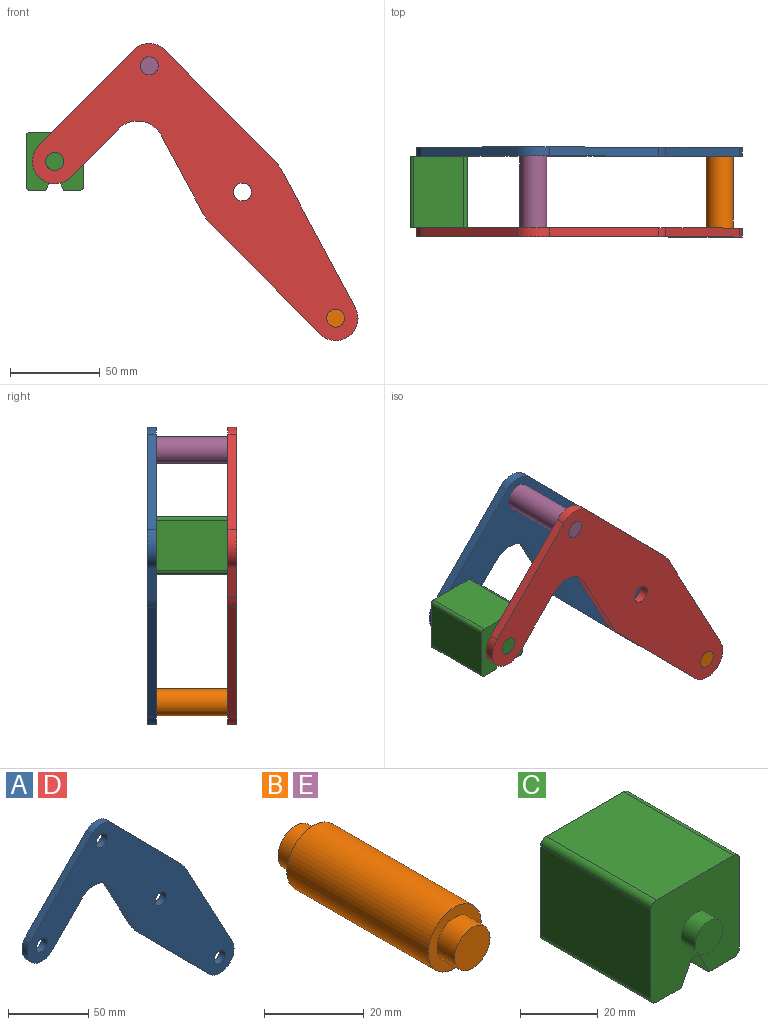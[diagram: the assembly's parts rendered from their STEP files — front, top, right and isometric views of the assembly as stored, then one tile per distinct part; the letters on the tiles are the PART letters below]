
ASSEMBLY  parts=5 mates=3
PART A: 18 faces, bbox 181.7x5x165.8 mm
  f0: plane 43.49x23.35mm, normal (-0.88,0,-0.47), area 246.8mm2, adj f1,f14,f16,f17
  f1: cylinder r=25mm len=5.75mm, axis (0,1,0), area 35.8mm2, adj f0,f2,f16,f17
  f2: plane 61.6x60.87mm, normal (-0.71,0,-0.7), area 433mm2, adj f1,f3,f16,f17
  f3: cylinder r=12.5mm len=21.39mm, axis (0,1,0), area 178.4mm2, adj f2,f4,f16,f17
  f4: plane 76.3x40.96mm, normal (0.88,0,0.47), area 433mm2, adj f3,f5,f16,f17
  f5: cylinder r=25mm len=5.75mm, axis (0,1,0), area 35.8mm2, adj f4,f6,f16,f17
  f6: plane 61.6x60.87mm, normal (0.71,0,0.7), area 433mm2, adj f5,f7,f16,f17
  f7: cylinder r=12.5mm len=17.78mm, axis (0,1,0), area 98.9mm2, adj f6,f8,f16,f17
  f8: plane 53.35x52.71mm, normal (-0.71,0,0.7), area 375mm2, adj f7,f9,f16,f17
  f9: cylinder r=12.5mm len=21.39mm, axis (0,1,0), area 196.3mm2, adj f8,f10,f16,f17
  f10: plane 26.86x26.54mm, normal (0.71,0,-0.7), area 188.8mm2, adj f9,f14,f16,f17
  f11: cylinder r=5mm len=10mm, axis (0,1,0), area 157.1mm2, adj f16,f17
  f12: cylinder r=5mm len=10mm, axis (0,1,0), area 157.1mm2, adj f16,f17
  f13: cylinder r=5mm len=10mm, axis (0,1,0), area 157.1mm2, adj f16,f17
  f14: cylinder r=15mm len=23.89mm, axis (0,1,0), area 140.2mm2, adj f0,f10,f16,f17
  f15: cylinder r=5mm len=10mm, axis (0,1,0), area 157.1mm2, adj f16,f17
  f16: plane 181.66x165.78mm, normal (0,-1,0), area 8710.1mm2, adj f0,f1,f2,f3,f4,f5,f6,f7
  f17: plane 181.66x165.78mm, normal (0,1,0), area 8710.1mm2, adj f0,f1,f2,f3,f4,f5,f6,f7
PART B: 7 faces, bbox 15x50x15 mm
  f0: cylinder r=7.5mm len=40mm, axis (0,-1,0), area 1885mm2, adj f2,f5
  f1: cylinder r=5mm len=10mm, axis (0,1,0), area 157.1mm2, adj f2,f3
  f2: plane 15x15mm, normal (0,-1,0), area 98.2mm2, adj f0,f1
  f3: plane 10x10mm, normal (0,-1,0), area 78.5mm2, adj f1
  f4: cylinder r=5mm len=10mm, axis (0,-1,0), area 157.1mm2, adj f5,f6
  f5: plane 15x15mm, normal (0,1,0), area 98.2mm2, adj f0,f4
  f6: plane 10x10mm, normal (0,1,0), area 78.5mm2, adj f4
PART C: 18 faces, bbox 32.1x50x32.1 mm
  f0: plane 40x28.08mm, normal (1,0,0), area 1123.1mm2, adj f4,f10,f13,f14
  f1: plane 40x9.04mm, normal (0,0,-1), area 361.6mm2, adj f2,f4,f10,f14
  f2: plane 40x6.42mm, normal (-0.89,0,-0.45), area 287.2mm2, adj f1,f4,f10,f15
  f3: plane 40x6.42mm, normal (0.89,0,-0.45), area 287.2mm2, adj f4,f5,f10,f15
  f4: plane 32.08x32.08mm, normal (0,-1,0), area 900.6mm2, adj f0,f1,f2,f3,f5,f6,f7,f9
  f5: plane 40x9.04mm, normal (0,0,-1), area 361.6mm2, adj f3,f4,f10,f16
  f6: plane 40x28.08mm, normal (0,0,1), area 1123.1mm2, adj f4,f10,f13,f17
  f7: plane 40x28.08mm, normal (-1,0,0), area 1123.1mm2, adj f4,f10,f16,f17
  f8: plane 10x10mm, normal (0,-1,0), area 78.5mm2, adj f9
  f9: cylinder r=5mm len=10mm, axis (0,1,0), area 157.1mm2, adj f4,f8
  f10: plane 32.08x32.08mm, normal (0,1,0), area 900.6mm2, adj f0,f1,f2,f3,f5,f6,f7,f12
  f11: plane 10x10mm, normal (0,1,0), area 78.5mm2, adj f12
  f12: cylinder r=5mm len=10mm, axis (0,-1,0), area 157.1mm2, adj f10,f11
  f13: cylinder r=2mm len=40mm, axis (0,1,0), area 125.7mm2, adj f0,f4,f6,f10
  f14: cylinder r=2mm len=40mm, axis (0,-1,0), area 125.7mm2, adj f0,f1,f4,f10
  f15: cylinder r=2mm len=40mm, axis (0,1,0), area 177.1mm2, adj f2,f3,f4,f10
  f16: cylinder r=2mm len=40mm, axis (0,1,0), area 125.7mm2, adj f4,f5,f7,f10
  f17: cylinder r=2mm len=40mm, axis (0,-1,0), area 125.7mm2, adj f4,f6,f7,f10
PART D: same geometry as A
PART E: same geometry as B
PLACE A t=(0,25,0)mm
PLACE B t=(103.95,-20,-140.78)mm
PLACE C t=(0,-20,0)mm
PLACE D t=(0,-20,0)mm fixed
PLACE E t=(0,-20,0)mm
MATE fastened B.f0 <-> D.f3  axis (0,1,0) through (51.98,-20,-70.39)mm
MATE revolute C.f9 <-> D.f9  axis (0,-1,0) through (-104.69,-20,17.04)mm
MATE fastened E.f0 <-> A.f7  axis (0,-1,0) through (-51.98,20,70.39)mm
